# Revit family: Hager-Orion_Plus-IP65-D300-Cl.II-Poly_floor_encl-630A-IT-it
name_source: partatom
category: Electrical Equipment
units: mm (PartAtom-declared; Revit-internal decimal feet)

## family parameters
Cut with Voids When Loaded = No
Host = Face
Panel Configuration = Two Columns, Circuits Across
Part Type = Panelboard
Room Calculation Point = No
Round Connector Dimension = Use Diameter
Shared = No

## types (9) — shared parameters
EF000003 - Tipo di montaggio = EV012274 - montaggio a pavimento
EF000007 - colore = EV000270 - grigio
EF000049 - profondità = 300 mm  [stored 0.984252 ft]
EF000116 - numero RAL = 7035
EF000118 - con piastra di montaggio = No
EF000339 - tipo di copertura = EV004216 - porta
EF001088 - possibilità di applicazione = Yes
EF001131 - profondità interna = 235 mm  [stored 0.770997 ft]
EF001596 - Attacco Lampada = EV000139 - plastica
EF001613 - Integrità del circuito = EV000494 - senza
EF003532 - adatto per uso esterno = Yes
EF004293 - resistenza agli urti = EV008784 - IK10
EF004464 - tipo di porta = EV000494 - senza
EF005474 - grado di protezione (IP) = EV006421 - IP65
EF006244 - coperchio/porta trasparente = No
EF006306 - con serratura = Yes
EF007800 - adatto per parafulmine = No
EF008873 - corrente nominale (In) = 630 A
EF009170 - spessore materiale scatola = 3 mm  [stored 0.00984252 ft]
EF009171 - spessore materiale porta/coperchio = 3 mm  [stored 0.00984252 ft]
EF009212 - esecuzione coperchio = EV000116 - chiuso
EF015940 - Coprire con rilascio di sovrapressione = No
HG000002 - Con porta = Yes
HG000003 - Gamma = Orion Plus
HG000006 - Ad incasso = No
HG000009 - Porta doppia a battente = No
HG000010 - Porte asimmetriche = No
HG000023 - Custodia a doppia sezione = No
HG000024 - Altezza della sezione inferiore = 800 mm  [stored 2.62467 ft]
HG000026 - A pavimento = Yes
HG000027 - Altezza dello zoccolo = 70 mm  [stored 0.229659 ft]
Manufacturer = Hager
Type Comments = Orion Plus
zero-valued in all types: Default Elevation, EF000218 - profondità di incasso, EF000437 - numero di ingressi per conduttori, EF009554 - numero delle aperture per la piastra della flangia

## per-type parameters (varying)
| type | EF000008 - Larghezza | EF000040 - Altezza | EF000266 - numero di file | EF002950 - Numero moduli DIN | EF004427 - numero di moduli | HG000004 - Codice produttore |
| montaggio a pavimento IP65 L1100 A1200 P300  - FL332BA | 1100 mm | 1200 mm | 7 | 46 | 322 | FL332BA |
| montaggio a pavimento IP65 L1100 A600 P300  - FL330BA | 1100 mm | 600 mm | 3 | 46 | 138 | FL330BA |
| montaggio a pavimento IP65 L1100 A900 P300  - FL331BA | 1100 mm | 900 mm  [stored 2.95276 ft] | 5 | 46 | 30 | FL331BA |
| montaggio a pavimento IP65 L600 A1200 P300  - FL322BA | 600 mm | 1200 mm | 7 | 23 | 161 | FL322BA |
| montaggio a pavimento IP65 L600 A600 P300  - FL320BA | 600 mm | 600 mm | 3 | 23 | 696 | FL320BA |
| montaggio a pavimento IP65 L600 A900 P300  - FL321BA | 600 mm | 900 mm  [stored 2.95276 ft] | 5 | 23 | 115 | FL321BA |
| montaggio a pavimento IP65 L850 A1200 P300  - FL327BA | 850 mm  [stored 2.78871 ft] | 1200 mm | 7 | 37 | 259 | FL327BA |
| montaggio a pavimento IP65 L850 A600 P300  - FL325BA | 850 mm  [stored 2.78871 ft] | 600 mm | 3 | 37 | 111 | FL325BA |
| montaggio a pavimento IP65 L850 A900 P300  - FL326BA | 850 mm  [stored 2.78871 ft] | 900 mm  [stored 2.95276 ft] | 5 | 37 | 185 | FL326BA |

note: [stored X ft] marks values corroborated as IEEE doubles in the binary element streams (Revit-internal decimal feet)

## geometry (parser evidence)
native form markers: Sweep x10
no freeform markers — native parametric forms only
